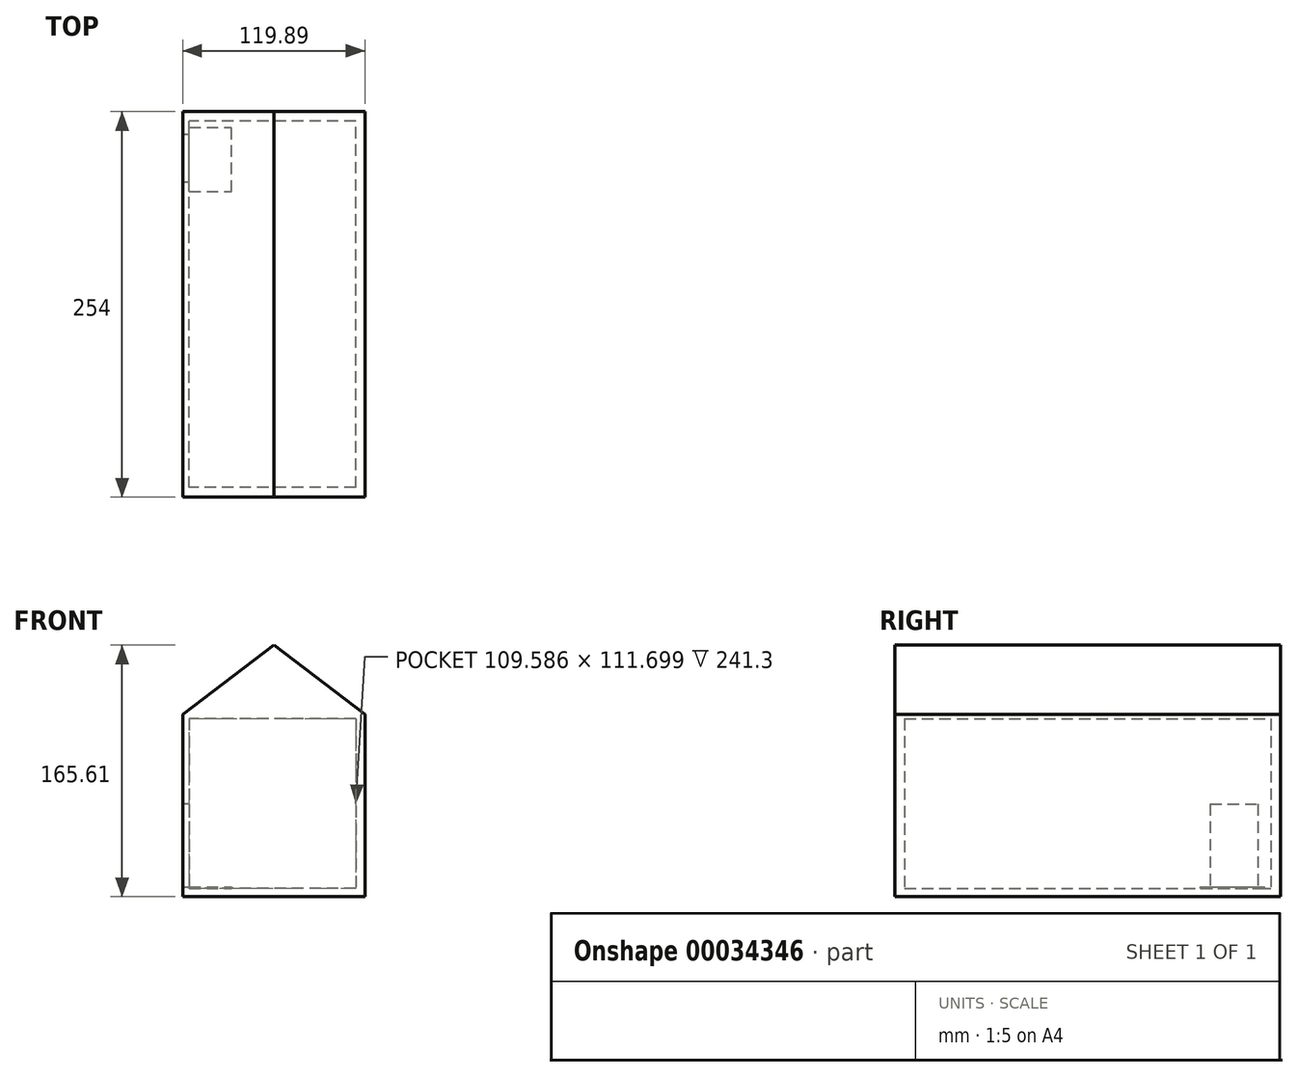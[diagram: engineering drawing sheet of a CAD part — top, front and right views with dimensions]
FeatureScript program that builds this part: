
annotation { "Feature Type Name" : "Feature", "Feature Type Description" : "" }
export const myFeature = defineFeature(function(context is Context, id is Id, definition is map)
    precondition{}
    {
        {
            var Q0;
            Q0=qCreatedBy(makeId("Front.planeOp"),FACE);
            var sketch = newSketch(context, id + "F0", { "sketchPlane" : qUnion([Q0])});
            skLineSegment(sketch, "E0.bottom", {"start": v(-76.17, 75.75) * mm, "end": v(43.72, 75.75) * mm});
            skLineSegment(sketch, "E0.top", {"start": v(-76.17, -44.14) * mm, "end": v(43.72, -44.14) * mm});
            skLineSegment(sketch, "E0.left", {"start": v(-76.17, 75.75) * mm, "end": v(-76.17, -44.14) * mm});
            skLineSegment(sketch, "E0.right", {"start": v(43.72, 75.75) * mm, "end": v(43.72, -44.14) * mm});
            skPoint(sketch, "E1", {"position": v(-16.23, 75.75) * mm});
            skLineSegment(sketch, "E2", {"start": v(-76.17, 75.75) * mm, "end": v(-16.23, 121.47) * mm});
            skLineSegment(sketch, "E3", {"start": v(-16.23, 121.47) * mm, "end": v(43.72, 75.75) * mm});
            skSolve(sketch);
        }
        {
            var Q0;
            Q0=makeQuery(id+"F0.imprint","IMPRINT",FACE,{"disambiguationData":[TD([[makeQuery(id+"F0.imprint","IMPRINT",EDGE,{"derivedFrom":sQuery(id+"F0.wireOp",EDGE,"E0.bottom")}),1.0]])]});
            var Q1;
            Q1=makeQuery(id+"F0.imprint","IMPRINT",FACE,{"disambiguationData":[TD([[makeQuery(id+"F0.imprint","IMPRINT",EDGE,{"derivedFrom":sQuery(id+"F0.wireOp",EDGE,"E0.bottom")}),-1.0]])]});
            extrude(context, id + "F1", {"entities" : qUnion([Q0, Q1]), "depth" : 254 * mm});
        }
        {
            var Q0;
            Q0=makeQuery(id+"F1.opExtrude","CAP_FACE",FACE,{"disambiguationData":[OSD([sQuery(id+"F0.wireOp",EDGE,"E0.top"),sQuery(id+"F0.wireOp",EDGE,"E0.left"),sQuery(id+"F0.wireOp",EDGE,"E0.right"),sQuery(id+"F0.wireOp",EDGE,"E2"),sQuery(id+"F0.wireOp",EDGE,"E3")])],"isStart":true});
            var sketch = newSketch(context, id + "F2", { "sketchPlane" : qUnion([Q0])});
            skLineSegment(sketch, "E4.bottom", {"start": v(-37.69, 73) * mm, "end": v(71.9, 73) * mm});
            skLineSegment(sketch, "E4.top", {"start": v(-37.69, -38.7) * mm, "end": v(71.9, -38.7) * mm});
            skLineSegment(sketch, "E4.left", {"start": v(-37.69, 73) * mm, "end": v(-37.69, -38.7) * mm});
            skLineSegment(sketch, "E4.right", {"start": v(71.9, 73) * mm, "end": v(71.9, -38.7) * mm});
            skSolve(sketch);
        }
        {
            var Q0;
            Q0 = qSketchRegion(id + "F2", true);
            extrude(context, id + "F3", {"entities" : qUnion([Q0]), "operationType" : NewBodyOperationType.REMOVE, "oppositeDirection" : true, "depth" : 247.65 * mm});
        }
        {
            var Q0;
            Q0=makeQuery(id+"F1.opExtrude","SWEPT_FACE",FACE,{"disambiguationData":[OSD([sQuery(id+"F0.wireOp",EDGE,"E0.left")])]});
            var sketch = newSketch(context, id + "F4", { "sketchPlane" : qUnion([Q0])});
            skLineSegment(sketch, "E5.bottom", {"start": v(14.89, -44.14) * mm, "end": v(46.24, -44.14) * mm});
            skLineSegment(sketch, "E5.top", {"start": v(14.89, 16.73) * mm, "end": v(46.24, 16.73) * mm});
            skLineSegment(sketch, "E5.left", {"start": v(14.89, -44.14) * mm, "end": v(14.89, 16.73) * mm});
            skLineSegment(sketch, "E5.right", {"start": v(46.24, -44.14) * mm, "end": v(46.24, 16.73) * mm});
            skSolve(sketch);
        }
        {
            var Q0;
            Q0=makeQuery(id+"F4.imprint","IMPRINT",FACE,{"disambiguationData":[TD([[makeQuery(id+"F4.imprint","IMPRINT",EDGE,{"derivedFrom":sQuery(id+"F4.wireOp",EDGE,"E5.bottom")}),-1.0]])]});
            extrude(context, id + "F5", {"entities" : qUnion([Q0]), "operationType" : NewBodyOperationType.REMOVE, "oppositeDirection" : true, "depth" : 25.4 * mm});
        }
        {
            var Q0;
            Q0=qCreatedBy(makeId("Front.planeOp"),FACE);
            var sketch = newSketch(context, id + "F6", { "sketchPlane" : qUnion([Q0])});
            skLineSegment(sketch, "E6.bottom", {"start": v(42.44, 74.86) * mm, "end": v(-74.03, 74.86) * mm});
            skLineSegment(sketch, "E6.top", {"start": v(42.44, -41.6) * mm, "end": v(-74.03, -41.6) * mm});
            skLineSegment(sketch, "E6.left", {"start": v(42.44, 74.86) * mm, "end": v(42.44, -41.6) * mm});
            skLineSegment(sketch, "E6.right", {"start": v(-74.03, 74.86) * mm, "end": v(-74.03, -41.6) * mm});
            skSolve(sketch);
        }
        {
            var Q0;
            Q0 = qSketchRegion(id + "F6", true);
            extrude(context, id + "F7", {"entities" : qUnion([Q0]), "operationType" : NewBodyOperationType.ADD, "depth" : 6.35 * mm});
        }
        {
            var Q0;
            Q0=makeQuery(id+"F1.opExtrude","SWEPT_FACE",FACE,{"disambiguationData":[OSD([sQuery(id+"F0.wireOp",EDGE,"E0.top")])]});
            var sketch = newSketch(context, id + "F8", { "sketchPlane" : qUnion([Q0])});
            skLineSegment(sketch, "E7.bottom", {"start": v(-76.17, 52.72) * mm, "end": v(-44.07, 52.72) * mm});
            skLineSegment(sketch, "E7.top", {"start": v(-76.17, 10.34) * mm, "end": v(-44.07, 10.34) * mm});
            skLineSegment(sketch, "E7.left", {"start": v(-76.17, 52.72) * mm, "end": v(-76.17, 10.34) * mm});
            skLineSegment(sketch, "E7.right", {"start": v(-44.07, 52.72) * mm, "end": v(-44.07, 10.34) * mm});
            skSolve(sketch);
        }
        {
            var Q0;
            Q0 = qSketchRegion(id + "F8", true);
            extrude(context, id + "F9", {"entities" : qUnion([Q0]), "operationType" : NewBodyOperationType.ADD, "oppositeDirection" : true, "depth" : 6.35 * mm});
        }
    });
